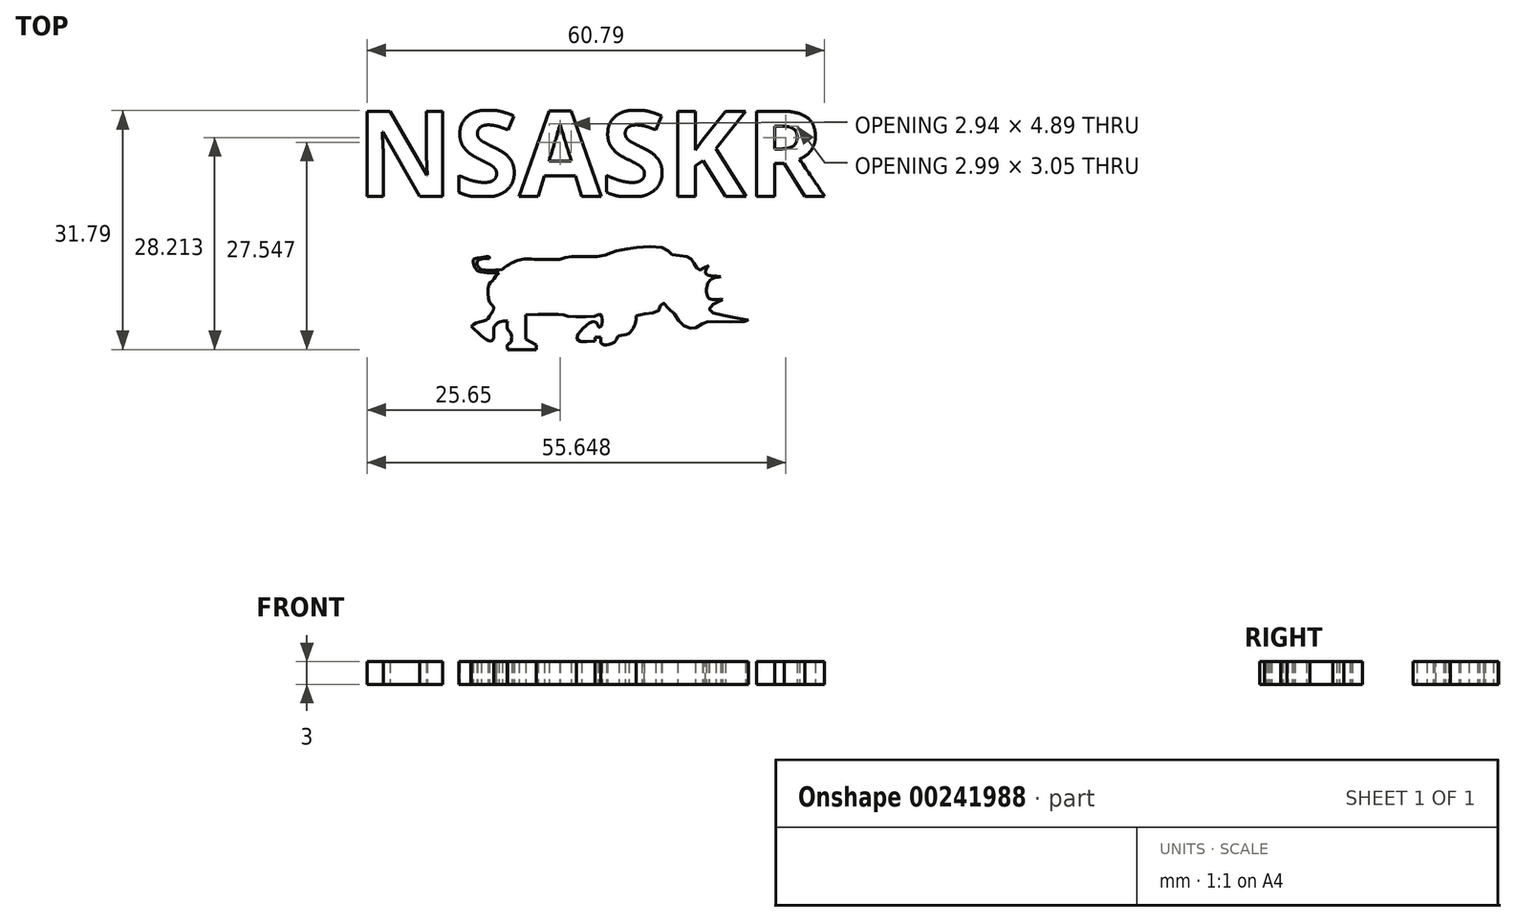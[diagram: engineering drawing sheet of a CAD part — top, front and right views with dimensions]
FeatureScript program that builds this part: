
annotation { "Feature Type Name" : "Feature", "Feature Type Description" : "" }
export const myFeature = defineFeature(function(context is Context, id is Id, definition is map)
    precondition{}
    {
        {
            var Q0;
            Q0=qCreatedBy(makeId("Top.planeOp"),FACE);
            var sketch = newSketch(context, id + "F0", { "sketchPlane" : qUnion([Q0])});
            skLineSegment(sketch, "E0.bottom", {"start": v(-14.56, 19.1) * mm, "end": v(48.67, 19.1) * mm});
            skLineSegment(sketch, "E0.top", {"start": v(-14.56, 7.7) * mm, "end": v(48.67, 7.7) * mm});
            skLineSegment(sketch, "E0.left", {"start": v(-14.56, 19.1) * mm, "end": v(-14.56, 7.7) * mm});
            skLineSegment(sketch, "E0.right", {"start": v(48.67, 19.1) * mm, "end": v(48.67, 7.7) * mm});
            skText(sketch, "E1", { "text": "NSASKR", "fontName": "OpenSans-Bold.ttf"});
            skFitSpline(sketch, "E2", {"points": [v(32.25, -1.5) * mm, v(31.5, -1.9) * mm, v(30.98, -2.1) * mm, v(30.45, -1.47) * mm, v(29.91, -0.67) * mm, v(29.12, -0.26) * mm, v(27.27, 0) * mm, v(26.44, 0.74) * mm, v(21.78, 0.78) * mm, v(20.63, 0.52) * mm, v(19.57, 0.3) * mm, v(18.24, -0.2) * mm, v(15.49, -0.34) * mm, v(13.67, -0.39) * mm, v(12.43, -0.68) * mm], "startDerivative": vector(-13.85, -6.83) * mm, "endDerivative": vector(-17.69, -5.15) * mm});
            skFitSpline(sketch, "E3", {"points": [v(12.43, -0.68) * mm, v(9.07, -0.68) * mm, v(7.52, -0.68) * mm, v(6.2, -1.13) * mm, v(5.22, -1.7) * mm, v(4.85, -2.05) * mm], "startDerivative": vector(-12.18, -0.2) * mm, "endDerivative": vector(-2.21, -4.1) * mm});
            skFitSpline(sketch, "E4", {"points": [v(4.85, -2.05) * mm, v(2.06, -2.05) * mm, v(1.64, -1.7) * mm, v(1.43, -1.15) * mm, v(1.83, -0.72) * mm, v(3.1, -0.56) * mm], "startDerivative": vector(-10.66, -1.14) * mm, "endDerivative": vector(6.2, 0.02) * mm});
            skFitSpline(sketch, "E5", {"points": [v(3.1, -0.56) * mm, v(3.1, -0.4) * mm, v(2.23, -0.4) * mm, v(1.4, -0.56) * mm, v(1, -0.73) * mm, v(1.03, -1.51) * mm, v(1.3, -2) * mm, v(1.94, -2.36) * mm, v(4.39, -2.46) * mm], "startDerivative": vector(1.09, 3.3) * mm, "endDerivative": vector(12.62, 0.3) * mm});
            skFitSpline(sketch, "E6", {"points": [v(4.39, -2.46) * mm, v(3.98, -2.94) * mm, v(3.44, -3.6) * mm, v(3.02, -4.13) * mm, v(3.06, -6.25) * mm, v(3.5, -6.8) * mm, v(3.68, -7.27) * mm, v(3.06, -8.3) * mm, v(2.71, -8.76) * mm, v(1.46, -9.1) * mm, v(0.72, -9.6) * mm], "startDerivative": vector(-4.71, -5.28) * mm, "endDerivative": vector(-6.17, -5.67) * mm});
            skFitSpline(sketch, "E7", {"points": [v(0.72, -9.6) * mm, v(3.29, -11.56) * mm, v(3.68, -10.94) * mm, v(3.68, -9.84) * mm, v(4.39, -9.06) * mm, v(5.52, -8.91) * mm], "startDerivative": vector(9.97, -9.84) * mm, "endDerivative": vector(6.42, -0.09) * mm});
            skFitSpline(sketch, "E8", {"points": [v(5.52, -8.91) * mm, v(5.52, -10) * mm, v(5.95, -10.53) * mm, v(5.93, -11.7) * mm, v(5.52, -12.08) * mm, v(5.52, -12.7) * mm], "startDerivative": vector(-0.8, -5.42) * mm, "endDerivative": vector(0.76, -4.06) * mm});
            skLineSegment(sketch, "E9", {"start": v(5.52, -12.7) * mm, "end": v(9.3, -12.7) * mm});
            skLineSegment(sketch, "E10", {"start": v(9.3, -12.7) * mm, "end": v(9.3, -12.06) * mm});
            skLineSegment(sketch, "E11", {"start": v(9.3, -12.06) * mm, "end": v(7.92, -11.32) * mm});
            skLineSegment(sketch, "E12", {"start": v(7.92, -11.32) * mm, "end": v(7.92, -8.05) * mm});
            skFitSpline(sketch, "E13", {"points": [v(7.92, -8.05) * mm, v(12.66, -8.05) * mm, v(13.58, -8.24) * mm, v(17.16, -8.22) * mm, v(17.9, -8.05) * mm, v(18.1, -8.76) * mm, v(17.9, -9.7) * mm, v(17.54, -9.68) * mm, v(17.48, -9.24) * mm, v(17.05, -9.02) * mm, v(16.53, -9.07) * mm, v(14.72, -10.92) * mm, v(15.01, -11.54) * mm, v(17.12, -11.58) * mm], "startDerivative": vector(38.7, 1.05) * mm, "endDerivative": vector(24.5, 2.4) * mm});
            skLineSegment(sketch, "E14", {"start": v(17.12, -11.58) * mm, "end": v(17.12, -11.08) * mm});
            skLineSegment(sketch, "E15", {"start": v(17.12, -11.08) * mm, "end": v(17.9, -11.08) * mm});
            skLineSegment(sketch, "E16", {"start": v(17.9, -11.08) * mm, "end": v(17.9, -11.82) * mm});
            skFitSpline(sketch, "E17", {"points": [v(17.9, -11.82) * mm, v(18.63, -12.08) * mm, v(19.93, -11.48) * mm, v(20.25, -10.88) * mm, v(21.43, -10.68) * mm, v(22.12, -9.97) * mm, v(22.56, -8.95) * mm, v(22.6, -8.18) * mm], "startDerivative": vector(4.92, -3.09) * mm, "endDerivative": vector(-0.22, 5.88) * mm});
            skFitSpline(sketch, "E18", {"points": [v(22.6, -8.18) * mm, v(24.3, -7.84) * mm, v(25.51, -7.61) * mm, v(25.77, -7.01) * mm, v(26.12, -6.46) * mm, v(26.8, -7.09) * mm, v(27.75, -8.03) * mm, v(28.6, -9.31) * mm, v(29.73, -9.84) * mm, v(30.43, -9.84) * mm, v(31.41, -9.27) * mm, v(32.09, -9.02) * mm, v(35.76, -9.04) * mm, v(37.5, -8.84) * mm, v(34.22, -8.18) * mm, v(32.44, -7.56) * mm, v(32.38, -7.09) * mm, v(34.1, -6.02) * mm], "startDerivative": vector(25.42, 6.1) * mm, "endDerivative": vector(31.88, 15.04) * mm});
            skFitSpline(sketch, "E19", {"points": [v(34.1, -6.02) * mm, v(32.26, -5.84) * mm, v(32.23, -3.7) * mm, v(33.86, -3) * mm], "startDerivative": vector(-6.46, 0.57) * mm, "endDerivative": vector(6.02, 0.83) * mm});
            skFitSpline(sketch, "E20", {"points": [v(32.25, -1.5) * mm, v(31.84, -2.57) * mm, v(33.86, -3) * mm], "startDerivative": vector(-1.9, -2.86) * mm, "endDerivative": vector(4.8, -0.25) * mm});
            const initialGuessF0  = {"E1": [-0.01456, 0.0077, 1, 0, 0.0114]};
            skSetInitialGuess(sketch, initialGuessF0);
            skSolve(sketch);
        }
        {
            var Q0;
            Q0=makeQuery(id+"F0.imprint","IMPRINT",FACE,{"disambiguationData":[TD([[makeQuery(id+"F0.imprint","IMPRINT",EDGE,{"derivedFrom":sQuery(id+"F0.wireOp",EDGE,"E1.sketch_text.stroke-82")}),-1.0]])]});
            var Q1;
            Q1=makeQuery(id+"F0.imprint","IMPRINT",FACE,{"disambiguationData":[TD([[makeQuery(id+"F0.imprint","IMPRINT",EDGE,{"derivedFrom":sQuery(id+"F0.wireOp",EDGE,"E1.sketch_text.stroke-95")}),-1.0]])]});
            var Q2;
            Q2=makeQuery(id+"F0.imprint","IMPRINT",FACE,{"disambiguationData":[TD([[makeQuery(id+"F0.imprint","IMPRINT",EDGE,{"derivedFrom":sQuery(id+"F0.wireOp",EDGE,"E1.sketch_text.stroke-0")}),-1.0]])]});
            var Q3;
            {var subQ12=sQuery(id+"F0.wireOp",EDGE,"E1.sketch_text.stroke-14");Q3=makeQuery(id+"F0.imprint","IMPRINT",FACE,{"disambiguationData":[TD([[makeQuery(id+"F0.imprint","IMPRINT",EDGE,{"derivedFrom":subQ12}),-1.0]])]});}
            var Q4;
            Q4=makeQuery(id+"F0.imprint","IMPRINT",FACE,{"disambiguationData":[TD([[makeQuery(id+"F0.imprint","IMPRINT",EDGE,{"derivedFrom":sQuery(id+"F0.wireOp",EDGE,"E1.sketch_text.stroke-42")}),-1.0]])]});
            var Q5;
            {var subQ6=sQuery(id+"F0.wireOp",EDGE,"E1.sketch_text.stroke-54");Q5=makeQuery(id+"F0.imprint","IMPRINT",FACE,{"disambiguationData":[TD([[makeQuery(id+"F0.imprint","IMPRINT",EDGE,{"derivedFrom":subQ6}),-1.0]])]});}
            var Q6;
            Q6=makeQuery(id+"F0.imprint","IMPRINT",FACE,{"disambiguationData":[TD([[makeQuery(id+"F0.imprint","IMPRINT",EDGE,{"derivedFrom":sQuery(id+"F0.wireOp",EDGE,"E2")}),1.0]])]});
            extrude(context, id + "F1", {"entities" : qUnion([Q0, Q1, Q2, Q3, Q4, Q5, Q6]), "depth" : 3 * mm});
        }
    });
